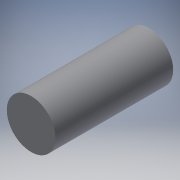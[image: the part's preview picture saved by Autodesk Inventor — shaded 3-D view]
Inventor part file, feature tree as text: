
AUTODESK INVENTOR PART (.ipt)
format: ipt  version: 2018.1 (Build 221171000, 171)  size: 91,648 bytes
history: native  units: mm
features: extrude x1, sketch x1
ambient origin geometry x8: Origin, YZ Plane, XZ Plane, XY Plane, X Axis, Y Axis, Z Axis, Center Point
bodies: Solid1 (feature_tree)
feature tree (2):
  extrude  "Extrusion1"  Depth=50.0mm TaperAngle=0.0deg
  sketch  "Sketch1"  dims[d0=20.6mm d1=50.0mm d2=0.0mm]
